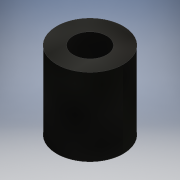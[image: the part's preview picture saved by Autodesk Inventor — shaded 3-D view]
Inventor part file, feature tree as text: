
AUTODESK INVENTOR PART (.ipt)
format: ipt  version: 2020.2 (Build 242310000, 310)  size: 94,720 bytes
history: native  units: mm
features: other x1, extrude x1, sketch x1
ambient origin geometry x8: Origin, YZ Plane, XZ Plane, XY Plane, X Axis, Y Axis, Z Axis, Center Point
bodies: Body1 (feature_tree)
feature tree (3):
  other  "ソリッド1"
  extrude  "押し出し1"  Depth=6.0mm
  sketch  "スケッチ1"
